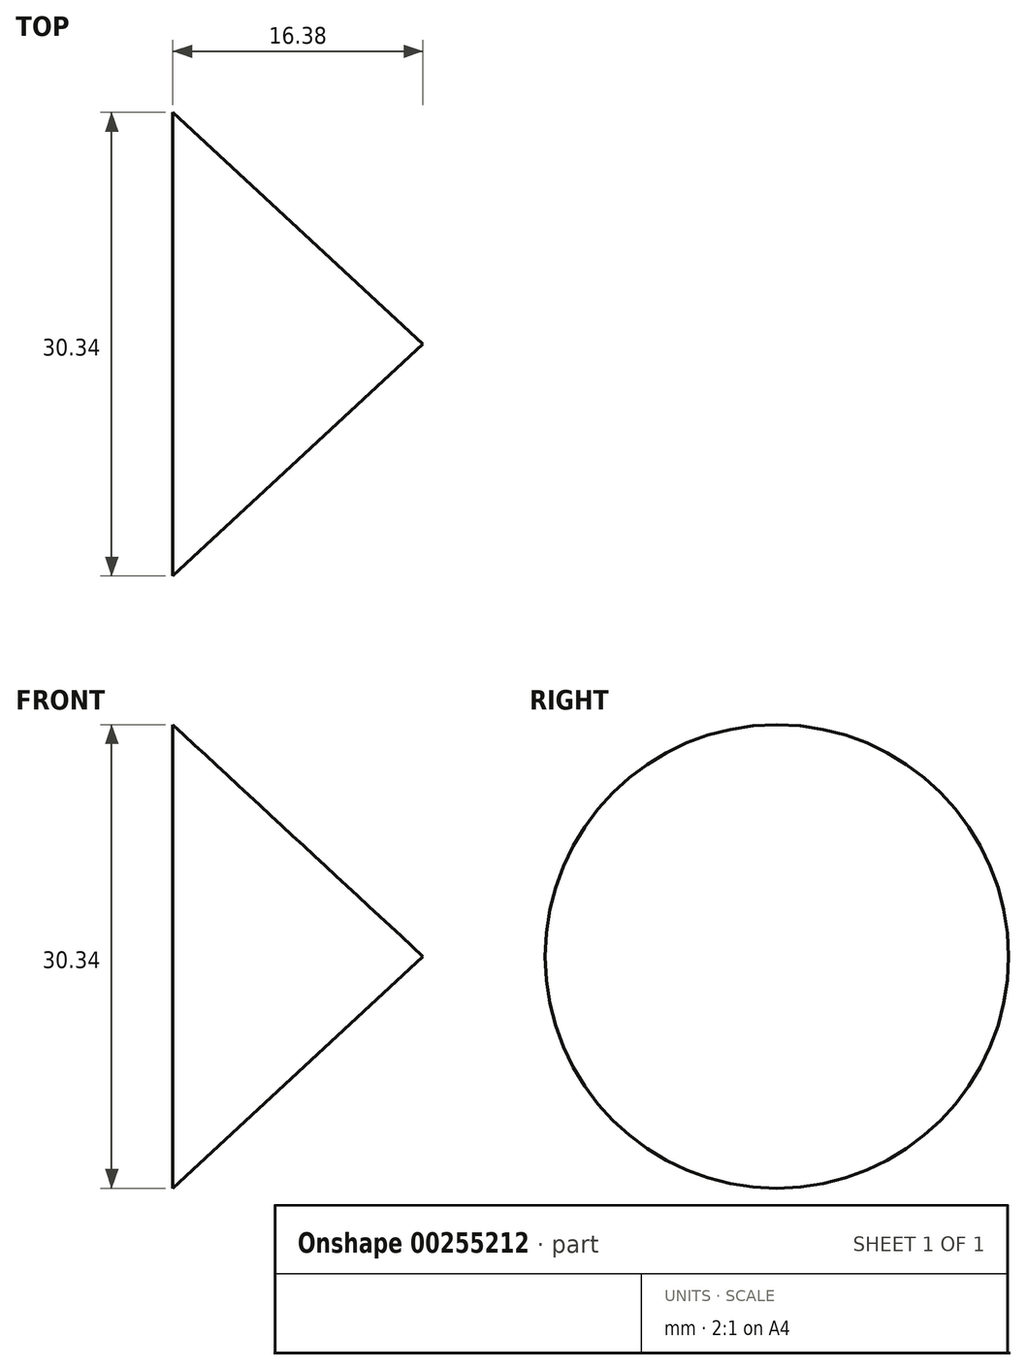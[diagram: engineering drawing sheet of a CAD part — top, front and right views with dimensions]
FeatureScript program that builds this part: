
annotation { "Feature Type Name" : "Feature", "Feature Type Description" : "" }
export const myFeature = defineFeature(function(context is Context, id is Id, definition is map)
    precondition{}
    {
        {
            var Q0;
            Q0=qCreatedBy(makeId("Front.planeOp"),FACE);
            var sketch = newSketch(context, id + "F0", { "sketchPlane" : qUnion([Q0])});
            skLineSegment(sketch, "E0", {"start": v(8, 0) * mm, "end": v(-7.86, 0) * mm});
            skArc(sketch, "E1", {"start": v(8, 0) * mm, "mid": v(5.66, 5.66) * mm, "end": v(0, 8) * mm});
            skLineSegment(sketch, "E2", {"start": v(0, 0) * mm, "end": v(0, 8) * mm});
            skPoint(sketch, "E3.orphan", {"position": v(-7.86, -1.46) * mm});
            skArc(sketch, "E4.MirrorCS", {"start": v(-8, 0) * mm, "mid": v(-5.66, 5.66) * mm, "end": v(0, 8) * mm});
            skSolve(sketch);
        }
        {
            var Q0;
            {var subQ0=sQuery(id+"F0.wireOp",EDGE,"E1");Q0=makeQuery(id+"F0.imprint","IMPRINT",FACE,{"disambiguationData":[TD([[makeQuery(id+"F0.imprint","IMPRINT",EDGE,{"derivedFrom":subQ0}),1.0]])]});}
            var sketch = newSketch(context, id + "F1", { "sketchPlane" : qUnion([Q0])});
            skLineSegment(sketch, "E5", {"start": v(0, 0) * mm, "end": v(-16.38, -15.17) * mm});
            skSolve(sketch);
        }
        {
            var Q0;
            Q0=sQuery(id+"F1.wireOp",EDGE,"E5");
            var Q1;
            Q1=sQuery(id+"F0.wireOp",EDGE,"E0");
            revolve(context, id + "F2", {"bodyType" : ToolBodyType.SURFACE, "surfaceEntities" : qUnion([Q0]), "axis" : qUnion([Q1]), "revolveType" : RevolveType.FULL});
        }
    });
